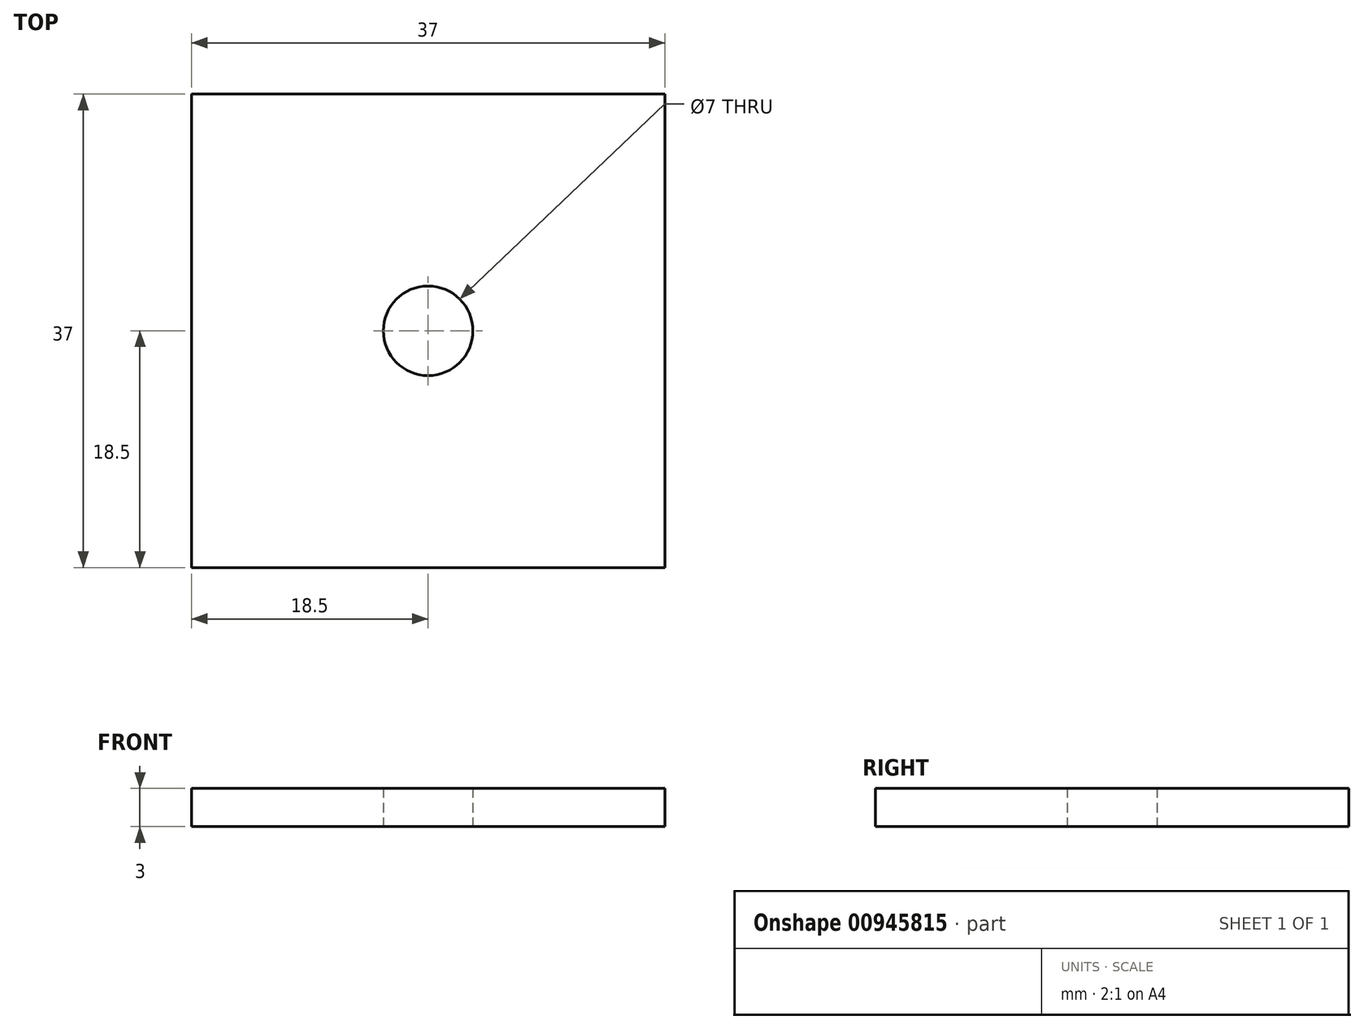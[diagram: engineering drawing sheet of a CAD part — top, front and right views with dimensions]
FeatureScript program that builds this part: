
annotation { "Feature Type Name" : "Feature", "Feature Type Description" : "" }
export const myFeature = defineFeature(function(context is Context, id is Id, definition is map)
    precondition{}
    {
        {
            var Q0;
            Q0=qCreatedBy(makeId("Top.planeOp"),FACE);
            var sketch = newSketch(context, id + "F0", { "sketchPlane" : qUnion([Q0])});
            skLineSegment(sketch, "E0.bottom", {"start": v(18.5, -18.5) * mm, "end": v(-18.5, -18.5) * mm});
            skLineSegment(sketch, "E0.top", {"start": v(18.5, 18.5) * mm, "end": v(-18.5, 18.5) * mm});
            skLineSegment(sketch, "E0.left", {"start": v(18.5, -18.5) * mm, "end": v(18.5, 18.5) * mm});
            skLineSegment(sketch, "E0.right", {"start": v(-18.5, -18.5) * mm, "end": v(-18.5, 18.5) * mm});
            skPoint(sketch, "E0.middle", {"position": v(0, 0) * mm});
            skCircle(sketch, "E1", {"center": v(0, 0) * mm, "radius": 3.5 * mm});
            skSolve(sketch);
        }
        {
            var Q0;
            Q0 = qSketchRegion(id + "F0", true);
            extrude(context, id + "F1", {"entities" : qUnion([Q0]), "depth" : 3 * mm, "offsetDistance" : 25 * mm});
        }
    });
